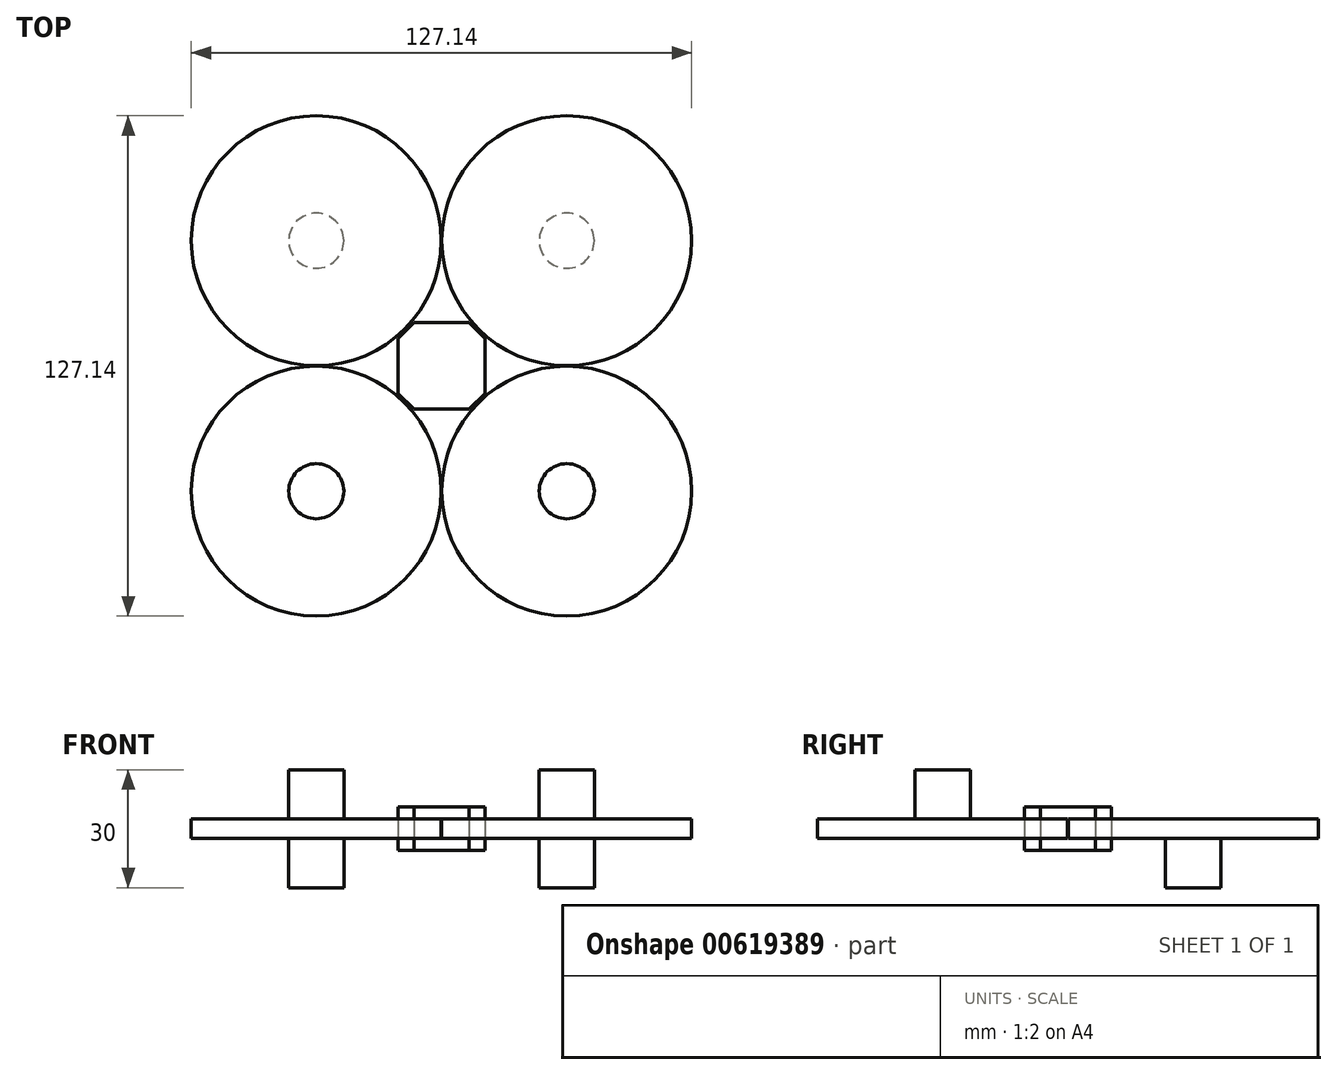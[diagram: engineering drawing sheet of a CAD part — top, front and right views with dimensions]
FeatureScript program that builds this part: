
annotation { "Feature Type Name" : "Feature", "Feature Type Description" : "" }
export const myFeature = defineFeature(function(context is Context, id is Id, definition is map)
    precondition{}
    {
        {
            var Q0;
            Q0=qCreatedBy(makeId("Top.planeOp"),FACE);
            var sketch = newSketch(context, id + "F0", { "sketchPlane" : qUnion([Q0])});
            skLineSegment(sketch, "E0.bottom", {"start": v(7, 11) * mm, "end": v(-7, 11) * mm});
            skLineSegment(sketch, "E0.top", {"start": v(7, -11) * mm, "end": v(-7, -11) * mm});
            skLineSegment(sketch, "E0.left", {"start": v(11, 7) * mm, "end": v(11, -7) * mm});
            skLineSegment(sketch, "E0.right", {"start": v(-11, 7) * mm, "end": v(-11, -7) * mm});
            skPoint(sketch, "E0.middle", {"position": v(0, 0) * mm});
            skLineSegment(sketch, "E1", {"start": v(0, 0) * mm, "end": v(31.82, -31.82) * mm, "construction": true});
            skLineSegment(sketch, "E2", {"start": v(0, 0) * mm, "end": v(31.82, 31.82) * mm, "construction": true});
            skLineSegment(sketch, "E3", {"start": v(0, 0) * mm, "end": v(-31.82, 31.82) * mm, "construction": true});
            skCircle(sketch, "E4", {"center": v(-31.82, -31.82) * mm, "radius": 31.75 * mm});
            skCircle(sketch, "E5", {"center": v(-31.82, 31.82) * mm, "radius": 31.75 * mm});
            skCircle(sketch, "E6", {"center": v(31.82, 31.82) * mm, "radius": 31.75 * mm});
            skCircle(sketch, "E7", {"center": v(31.82, -31.82) * mm, "radius": 31.75 * mm});
            skLineSegment(sketch, "E8", {"start": v(0, 0) * mm, "end": v(-31.82, -31.82) * mm, "construction": true});
            skLineSegment(sketch, "E9", {"start": v(-11, 7) * mm, "end": v(-7, 11) * mm});
            skLineSegment(sketch, "E10", {"start": v(-11, -7) * mm, "end": v(-7, -11) * mm});
            skLineSegment(sketch, "E11", {"start": v(7, 11) * mm, "end": v(11, 7) * mm});
            skLineSegment(sketch, "E12", {"start": v(11, -7) * mm, "end": v(7, -11) * mm});
            skSolve(sketch);
        }
        {
            var Q0;
            Q0=makeQuery(id+"F0.imprint","IMPRINT",FACE,{"disambiguationData":[TD([[makeQuery(id+"F0.imprint","IMPRINT",EDGE,{"derivedFrom":sQuery(id+"F0.wireOp",EDGE,"E4")}),1.0]])]});
            var Q1;
            Q1=makeQuery(id+"F0.imprint","IMPRINT",FACE,{"disambiguationData":[TD([[makeQuery(id+"F0.imprint","IMPRINT",EDGE,{"derivedFrom":sQuery(id+"F0.wireOp",EDGE,"E5")}),1.0]])]});
            var Q2;
            Q2=makeQuery(id+"F0.imprint","IMPRINT",FACE,{"disambiguationData":[TD([[makeQuery(id+"F0.imprint","IMPRINT",EDGE,{"derivedFrom":sQuery(id+"F0.wireOp",EDGE,"E6")}),1.0]])]});
            var Q3;
            Q3=makeQuery(id+"F0.imprint","IMPRINT",FACE,{"disambiguationData":[TD([[makeQuery(id+"F0.imprint","IMPRINT",EDGE,{"derivedFrom":sQuery(id+"F0.wireOp",EDGE,"E7")}),1.0]])]});
            extrude(context, id + "F1", {"entities" : qUnion([Q0, Q1, Q2, Q3]), "depth" : 5 * mm, "offsetDistance" : 25 * mm, "symmetric" : true});
        }
        {
            var Q0;
            Q0=makeQuery(id+"F1.opExtrude","CAP_FACE",FACE,{"disambiguationData":[OSD([sQuery(id+"F0.wireOp",EDGE,"E4")])],"isStart":false});
            var sketch = newSketch(context, id + "F2", { "sketchPlane" : qUnion([Q0])});
            skCircle(sketch, "E13", {"center": v(-31.82, -31.82) * mm, "radius": 7 * mm});
            skSolve(sketch);
        }
        {
            var Q0;
            Q0=makeQuery(id+"F2.imprint","IMPRINT",FACE,{"disambiguationData":[TD([[makeQuery(id+"F2.imprint","IMPRINT",EDGE,{"derivedFrom":sQuery(id+"F2.wireOp",EDGE,"E13")}),1.0]])]});
            var Q1;
            Q1=sQuery(id+"F2.wireOp",EDGE,"E13");
            extrude(context, id + "F3", {"entities" : qUnion([Q0]), "surfaceEntities" : qUnion([Q1]), "depth" : 12.5 * mm, "offsetDistance" : 25 * mm});
        }
        {
            var Q0;
            Q0=makeQuery(id+"F1.opExtrude","CAP_FACE",FACE,{"disambiguationData":[OSD([sQuery(id+"F0.wireOp",EDGE,"E7")])],"isStart":false});
            var sketch = newSketch(context, id + "F4", { "sketchPlane" : qUnion([Q0])});
            skCircle(sketch, "E14", {"center": v(31.82, -31.82) * mm, "radius": 7 * mm});
            skSolve(sketch);
        }
        {
            var Q0;
            Q0=makeQuery(id+"F4.imprint","IMPRINT",FACE,{"disambiguationData":[TD([[makeQuery(id+"F4.imprint","IMPRINT",EDGE,{"derivedFrom":sQuery(id+"F4.wireOp",EDGE,"E14")}),1.0]])]});
            extrude(context, id + "F5", {"entities" : qUnion([Q0]), "depth" : 12.5 * mm, "offsetDistance" : 25 * mm});
        }
        {
            var Q0;
            Q0=makeQuery(id+"F1.opExtrude","CAP_FACE",FACE,{"disambiguationData":[OSD([sQuery(id+"F0.wireOp",EDGE,"E5")])],"isStart":true});
            var sketch = newSketch(context, id + "F6", { "sketchPlane" : qUnion([Q0])});
            skCircle(sketch, "E15", {"center": v(-31.82, -31.82) * mm, "radius": 7 * mm});
            skSolve(sketch);
        }
        {
            var Q0;
            Q0=qSketchRegion(id+"F6",true);
            extrude(context, id + "F7", {"entities" : qUnion([Q0]), "depth" : 12.5 * mm, "offsetDistance" : 25 * mm});
        }
        {
            var Q0;
            Q0=makeQuery(id+"F1.opExtrude","CAP_FACE",FACE,{"disambiguationData":[OSD([sQuery(id+"F0.wireOp",EDGE,"E6")])],"isStart":true});
            var sketch = newSketch(context, id + "F8", { "sketchPlane" : qUnion([Q0])});
            skCircle(sketch, "E16", {"center": v(31.82, -31.82) * mm, "radius": 7 * mm});
            skSolve(sketch);
        }
        {
            var Q0;
            Q0=makeQuery(id+"F8.imprint","IMPRINT",FACE,{"disambiguationData":[TD([[makeQuery(id+"F8.imprint","IMPRINT",EDGE,{"derivedFrom":sQuery(id+"F8.wireOp",EDGE,"E16")}),1.0]])]});
            extrude(context, id + "F9", {"entities" : qUnion([Q0]), "depth" : 12.5 * mm, "offsetDistance" : 25 * mm});
        }
        {
            var Q0;
            Q0=makeQuery(id+"F0.imprint","IMPRINT",FACE,{"disambiguationData":[TD([[makeQuery(id+"F0.imprint","IMPRINT",EDGE,{"derivedFrom":sQuery(id+"F0.wireOp",EDGE,"E0.bottom")}),1.0]])]});
            extrude(context, id + "F10", {"entities" : qUnion([Q0]), "depth" : 11 * mm, "offsetDistance" : 25 * mm, "symmetric" : true});
        }
    });
